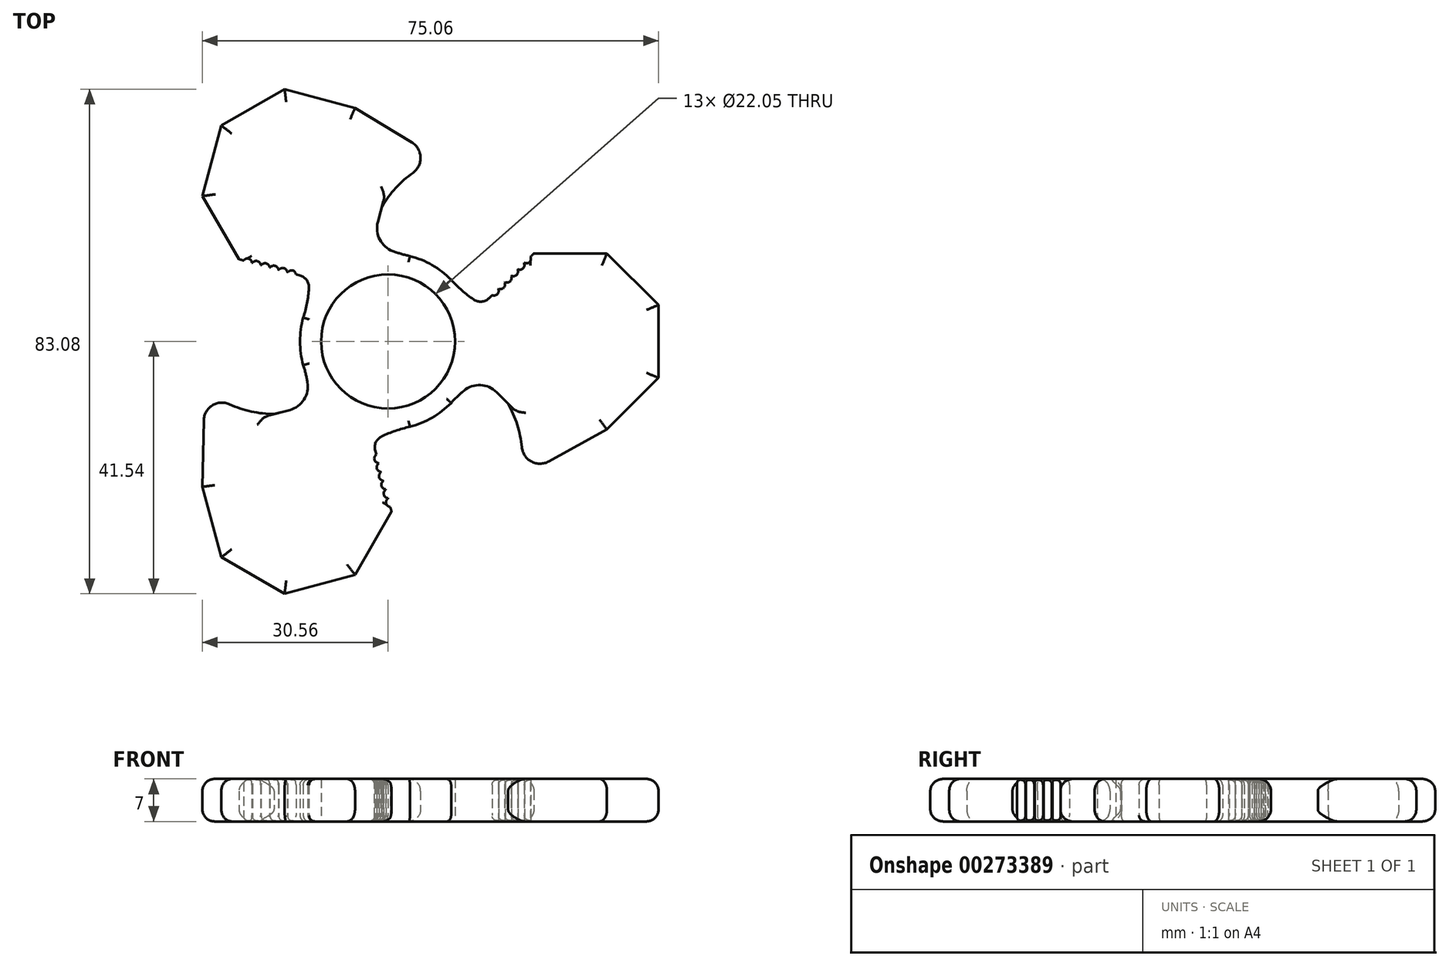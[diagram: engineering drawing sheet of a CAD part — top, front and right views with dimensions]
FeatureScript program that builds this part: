
annotation { "Feature Type Name" : "Feature", "Feature Type Description" : "" }
export const myFeature = defineFeature(function(context is Context, id is Id, definition is map)
    precondition{}
    {
        {
            var Q0;
            Q0=qCreatedBy(makeId("Top.planeOp"),FACE);
            var sketch = newSketch(context, id + "F0", { "sketchPlane" : qUnion([Q0])});
            skCircle(sketch, "E0", {"center": v(0, 0) * mm, "radius": 11.03 * mm});
            skLineSegment(sketch, "E1", {"start": v(30, 25.22) * mm, "end": v(30, -27.35) * mm, "construction": true});
            skCircle(sketch, "E2.cCircle", {"center": v(30, 0) * mm, "radius": 14.5 * mm, "construction": true});
            skLineSegment(sketch, "E2.2", {"start": v(24, 14.5) * mm, "end": v(36, 14.5) * mm});
            skLineSegment(sketch, "E2.3", {"start": v(36, 14.5) * mm, "end": v(44.5, 6) * mm});
            skLineSegment(sketch, "E2.4", {"start": v(44.5, 6) * mm, "end": v(44.5, -6) * mm});
            skLineSegment(sketch, "E2.5", {"start": v(44.5, -6) * mm, "end": v(36, -14.5) * mm});
            skLineSegment(sketch, "E2.7", {"start": v(19.75, -10.25) * mm, "end": v(17.86, -8.36) * mm});
            skPoint(sketch, "E2.0.midPoint", {"position": v(15.5, 0) * mm});
            skLineSegment(sketch, "E3", {"start": v(15.5, 6.36) * mm, "end": v(23.64, 14.5) * mm, "construction": true});
            skArc(sketch, "E4", {"start": v(17.12, 7.63) * mm, "mid": v(17.97, 7.77) * mm, "end": v(18.12, 8.63) * mm});
            skArc(sketch, "E5", {"start": v(18.18, 8.69) * mm, "mid": v(19.04, 8.83) * mm, "end": v(19.18, 9.69) * mm});
            skArc(sketch, "E6", {"start": v(19.24, 9.75) * mm, "mid": v(20.1, 9.9) * mm, "end": v(20.24, 10.75) * mm});
            skArc(sketch, "E7", {"start": v(20.3, 10.8) * mm, "mid": v(21.16, 10.96) * mm, "end": v(21.3, 11.8) * mm});
            skArc(sketch, "E8", {"start": v(21.36, 11.87) * mm, "mid": v(22.22, 12.02) * mm, "end": v(22.36, 12.87) * mm});
            skArc(sketch, "E9", {"start": v(22.42, 12.93) * mm, "mid": v(23.28, 13.08) * mm, "end": v(23.42, 13.93) * mm});
            skLineSegment(sketch, "E10.trimOffspring", {"start": v(18.12, 8.63) * mm, "end": v(18.18, 8.69) * mm});
            skLineSegment(sketch, "E11.trimOffspring", {"start": v(21.3, 11.8) * mm, "end": v(21.36, 11.87) * mm});
            skLineSegment(sketch, "E12.trimOffspring", {"start": v(22.36, 12.87) * mm, "end": v(22.42, 12.93) * mm});
            skLineSegment(sketch, "E13.trimOffspring", {"start": v(20.24, 10.75) * mm, "end": v(20.3, 10.8) * mm});
            skLineSegment(sketch, "E14.trimOffspring", {"start": v(19.18, 9.69) * mm, "end": v(19.24, 9.75) * mm});
            skLineSegment(sketch, "E15.trimOffspring", {"start": v(23.42, 13.93) * mm, "end": v(24, 14.5) * mm});
            skLineSegment(sketch, "E16", {"start": v(36, -14.5) * mm, "end": v(26.43, -19.76) * mm});
            skArc(sketch, "E17", {"start": v(22, -17.43) * mm, "mid": v(21.24, -13.73) * mm, "end": v(19.75, -10.25) * mm});
            skPoint(sketch, "E18.visualSharp", {"position": v(21.86, -22.27) * mm});
            skArc(sketch, "E18.filletArc", {"start": v(22, -17.43) * mm, "mid": v(23.6, -19.78) * mm, "end": v(26.43, -19.76) * mm});
            skPoint(sketch, "E19.orphan", {"position": v(24, -14.5) * mm});
            skArc(sketch, "E20", {"start": v(10.37, 10.14) * mm, "mid": v(6.97, 12.71) * mm, "end": v(2.98, 14.2) * mm});
            skArc(sketch, "E21", {"start": v(10.37, 10.14) * mm, "mid": v(12.13, 8.4) * mm, "end": v(14.08, 6.9) * mm});
            skArc(sketch, "E22.MirrorCS", {"start": v(10.37, -10.14) * mm, "mid": v(11.38, -9.1) * mm, "end": v(12.46, -8.12) * mm});
            skPoint(sketch, "E23.1.0", {"position": v(0.56, 28.03) * mm});
            skArc(sketch, "E23.1.1", {"start": v(4.1, 27.77) * mm, "mid": v(1.27, 25.26) * mm, "end": v(-1, 22.23) * mm});
            skLineSegment(sketch, "E23.1.2", {"start": v(-5.45, 38.43) * mm, "end": v(3.9, 32.77) * mm});
            skCircle(sketch, "E23.1.3", {"center": v(-15, 25.98) * mm, "radius": 14.5 * mm, "construction": true});
            skArc(sketch, "E23.1.4", {"start": v(3.6, 14.05) * mm, "mid": v(2.18, 14.4) * mm, "end": v(0.8, 14.86) * mm});
            skArc(sketch, "E23.1.5", {"start": v(4.1, 27.77) * mm, "mid": v(5.34, 30.33) * mm, "end": v(3.9, 32.77) * mm});
            skPoint(sketch, "E23.1.6", {"position": v(-7.75, 13.42) * mm});
            skPoint(sketch, "E23.1.7", {"position": v(8.36, 30.07) * mm});
            skLineSegment(sketch, "E23.1.8", {"start": v(-36.84, 13.37) * mm, "end": v(8.69, 39.66) * mm, "construction": true});
            skLineSegment(sketch, "E23.1.10", {"start": v(-24.55, 13.53) * mm, "end": v(-30.56, 23.93) * mm});
            skLineSegment(sketch, "E23.1.11", {"start": v(-1, 22.23) * mm, "end": v(-1.69, 19.65) * mm});
            skArc(sketch, "E23.1.12", {"start": v(-13.96, 3.91) * mm, "mid": v(-13.35, 6.3) * mm, "end": v(-13.01, 8.75) * mm});
            skLineSegment(sketch, "E23.1.13", {"start": v(-30.56, 23.93) * mm, "end": v(-27.45, 35.54) * mm});
            skLineSegment(sketch, "E23.1.14", {"start": v(-27.45, 35.54) * mm, "end": v(-17.05, 41.54) * mm});
            skLineSegment(sketch, "E23.1.15", {"start": v(-17.05, 41.54) * mm, "end": v(-5.45, 38.43) * mm});
            skArc(sketch, "E23.1.16", {"start": v(-18.06, 11.8) * mm, "mid": v(-18.62, 12.46) * mm, "end": v(-19.43, 12.16) * mm});
            skLineSegment(sketch, "E23.1.17", {"start": v(-19.43, 12.16) * mm, "end": v(-19.51, 12.18) * mm});
            skLineSegment(sketch, "E23.1.18", {"start": v(-13.26, 10.24) * mm, "end": v(-24.38, 13.22) * mm, "construction": true});
            skArc(sketch, "E23.1.20", {"start": v(-22.41, 12.95) * mm, "mid": v(-22.96, 13.62) * mm, "end": v(-23.78, 13.32) * mm});
            skArc(sketch, "E23.1.22", {"start": v(-15.17, 11.01) * mm, "mid": v(-15.72, 11.68) * mm, "end": v(-16.53, 11.38) * mm});
            skArc(sketch, "E23.1.23", {"start": v(-19.51, 12.18) * mm, "mid": v(-20.07, 12.84) * mm, "end": v(-20.88, 12.54) * mm});
            skLineSegment(sketch, "E23.1.24", {"start": v(-23.78, 13.32) * mm, "end": v(-24.55, 13.53) * mm});
            skArc(sketch, "E23.1.26", {"start": v(-16.62, 11.4) * mm, "mid": v(-17.17, 12.07) * mm, "end": v(-17.98, 11.77) * mm});
            skLineSegment(sketch, "E23.1.27", {"start": v(-17.98, 11.77) * mm, "end": v(-18.06, 11.8) * mm});
            skArc(sketch, "E23.1.28", {"start": v(-20.96, 12.57) * mm, "mid": v(-21.52, 13.23) * mm, "end": v(-22.33, 12.93) * mm});
            skLineSegment(sketch, "E23.1.29", {"start": v(-16.53, 11.38) * mm, "end": v(-16.62, 11.4) * mm});
            skLineSegment(sketch, "E23.1.30", {"start": v(-20.88, 12.54) * mm, "end": v(-20.96, 12.57) * mm});
            skLineSegment(sketch, "E23.1.31", {"start": v(-22.33, 12.93) * mm, "end": v(-22.41, 12.95) * mm});
            skPoint(sketch, "E23.2.0", {"position": v(-24.55, -13.53) * mm});
            skArc(sketch, "E23.2.1", {"start": v(-26.1, -10.34) * mm, "mid": v(-22.5, -11.53) * mm, "end": v(-18.75, -11.97) * mm});
            skLineSegment(sketch, "E23.2.2", {"start": v(-30.56, -23.93) * mm, "end": v(-30.33, -13.01) * mm});
            skCircle(sketch, "E23.2.3", {"center": v(-15, -25.98) * mm, "radius": 14.5 * mm, "construction": true});
            skArc(sketch, "E23.2.4", {"start": v(-13.96, -3.91) * mm, "mid": v(-13.57, -5.3) * mm, "end": v(-13.27, -6.73) * mm});
            skArc(sketch, "E23.2.5", {"start": v(-26.1, -10.34) * mm, "mid": v(-28.93, -10.54) * mm, "end": v(-30.33, -13.01) * mm});
            skPoint(sketch, "E23.2.6", {"position": v(-7.75, -13.42) * mm});
            skPoint(sketch, "E23.2.7", {"position": v(-30.22, -7.8) * mm});
            skLineSegment(sketch, "E23.2.8", {"start": v(6.84, -38.6) * mm, "end": v(-38.69, -12.3) * mm, "construction": true});
            skLineSegment(sketch, "E23.2.10", {"start": v(0.56, -28.03) * mm, "end": v(-5.45, -38.43) * mm});
            skLineSegment(sketch, "E23.2.11", {"start": v(-18.75, -11.97) * mm, "end": v(-16.17, -11.28) * mm});
            skArc(sketch, "E23.2.12", {"start": v(3.6, -14.05) * mm, "mid": v(1.22, -14.71) * mm, "end": v(-1.07, -15.64) * mm});
            skLineSegment(sketch, "E23.2.13", {"start": v(-5.45, -38.43) * mm, "end": v(-17.05, -41.54) * mm});
            skLineSegment(sketch, "E23.2.14", {"start": v(-17.05, -41.54) * mm, "end": v(-27.45, -35.54) * mm});
            skLineSegment(sketch, "E23.2.15", {"start": v(-27.45, -35.54) * mm, "end": v(-30.56, -23.93) * mm});
            skArc(sketch, "E23.2.16", {"start": v(-1.18, -21.54) * mm, "mid": v(-1.48, -22.35) * mm, "end": v(-0.81, -22.9) * mm});
            skLineSegment(sketch, "E23.2.17", {"start": v(-0.81, -22.9) * mm, "end": v(-0.8, -22.99) * mm});
            skLineSegment(sketch, "E23.2.18", {"start": v(-2.24, -16.6) * mm, "end": v(0.74, -27.72) * mm, "construction": true});
            skArc(sketch, "E23.2.20", {"start": v(-0.01, -25.89) * mm, "mid": v(-0.31, -26.7) * mm, "end": v(0.35, -27.25) * mm});
            skArc(sketch, "E23.2.22", {"start": v(-1.96, -18.64) * mm, "mid": v(-2.26, -19.45) * mm, "end": v(-1.59, -20) * mm});
            skArc(sketch, "E23.2.23", {"start": v(-0.8, -22.99) * mm, "mid": v(-1.1, -23.8) * mm, "end": v(-0.42, -24.35) * mm});
            skLineSegment(sketch, "E23.2.24", {"start": v(0.35, -27.25) * mm, "end": v(0.56, -28.03) * mm});
            skArc(sketch, "E23.2.26", {"start": v(-1.57, -20.1) * mm, "mid": v(-1.87, -20.9) * mm, "end": v(-1.2, -21.46) * mm});
            skLineSegment(sketch, "E23.2.27", {"start": v(-1.2, -21.46) * mm, "end": v(-1.18, -21.54) * mm});
            skArc(sketch, "E23.2.28", {"start": v(-0.4, -24.44) * mm, "mid": v(-0.7, -25.25) * mm, "end": v(-0.04, -25.8) * mm});
            skLineSegment(sketch, "E23.2.29", {"start": v(-1.59, -20) * mm, "end": v(-1.57, -20.1) * mm});
            skLineSegment(sketch, "E23.2.30", {"start": v(-0.42, -24.35) * mm, "end": v(-0.4, -24.44) * mm});
            skLineSegment(sketch, "E23.2.31", {"start": v(-0.04, -25.8) * mm, "end": v(-0.01, -25.89) * mm});
            skPoint(sketch, "E24.visualSharp", {"position": v(-2.55, 16.43) * mm});
            skArc(sketch, "E24.filletArc", {"start": v(-1.69, 19.65) * mm, "mid": v(-1.37, 16.77) * mm, "end": v(0.8, 14.86) * mm});
            skPoint(sketch, "E25.visualSharp", {"position": v(-12.95, -10.42) * mm});
            skArc(sketch, "E25.filletArc", {"start": v(-16.17, -11.28) * mm, "mid": v(-13.84, -9.57) * mm, "end": v(-13.27, -6.73) * mm});
            skPoint(sketch, "E26.visualSharp", {"position": v(15.5, -6) * mm});
            skArc(sketch, "E26.filletArc", {"start": v(17.86, -8.36) * mm, "mid": v(15.2, -7.2) * mm, "end": v(12.46, -8.12) * mm});
            skArc(sketch, "E27.trimOffspring", {"start": v(-13.78, 4.52) * mm, "mid": v(-14.5, 0) * mm, "end": v(-13.78, -4.52) * mm});
            skArc(sketch, "E28.trimOffspring", {"start": v(2.98, -14.2) * mm, "mid": v(6.97, -12.71) * mm, "end": v(10.37, -10.14) * mm});
            skPoint(sketch, "E29.visualSharp", {"position": v(15.5, 6) * mm});
            skArc(sketch, "E29.filletArc", {"start": v(14.08, 6.9) * mm, "mid": v(15.4, 6.56) * mm, "end": v(16.63, 7.13) * mm});
            skPoint(sketch, "E30.center.orphan", {"position": v(16.38, 7.24) * mm});
            skPoint(sketch, "E31.visualSharp", {"position": v(-2.55, -16.43) * mm});
            skArc(sketch, "E31.filletArc", {"start": v(-1.07, -15.64) * mm, "mid": v(-2.02, -16.61) * mm, "end": v(-2.14, -17.97) * mm});
            skLineSegment(sketch, "E32", {"start": v(-2.14, -17.97) * mm, "end": v(-1.96, -18.64) * mm});
            skLineSegment(sketch, "E33", {"start": v(16.63, 7.13) * mm, "end": v(17.12, 7.63) * mm});
            skPoint(sketch, "E34.visualSharp", {"position": v(-12.95, 10.42) * mm});
            skArc(sketch, "E34.filletArc", {"start": v(-13.01, 8.75) * mm, "mid": v(-13.38, 10.06) * mm, "end": v(-14.5, 10.83) * mm});
            skLineSegment(sketch, "E35", {"start": v(-14.5, 10.83) * mm, "end": v(-15.17, 11.01) * mm});
            skSolve(sketch);
        }
        {
            var Q0;
            Q0=makeQuery(id+"F0.imprint","IMPRINT",FACE,{"disambiguationData":[TD([[makeQuery(id+"F0.imprint","IMPRINT",EDGE,{"derivedFrom":sQuery(id+"F0.wireOp",EDGE,"E0")}),-1.0]])]});
            extrude(context, id + "F1", {"entities" : qUnion([Q0]), "depth" : 7 * mm});
        }
        {
            var Q0;
            Q0=makeQuery(id+"F1.opExtrude","CAP_EDGE",EDGE,{"disambiguationData":[OSD([sQuery(id+"F0.wireOp",EDGE,"E23.1.13")])],"isStart":false});
            var Q1;
            Q1=makeQuery(id+"F1.opExtrude","CAP_EDGE",EDGE,{"disambiguationData":[OSD([sQuery(id+"F0.wireOp",EDGE,"E23.1.14")])],"isStart":false});
            var Q2;
            Q2=makeQuery(id+"F1.opExtrude","CAP_EDGE",EDGE,{"disambiguationData":[OSD([sQuery(id+"F0.wireOp",EDGE,"E23.1.15")])],"isStart":false});
            var Q3;
            Q3=makeQuery(id+"F1.opExtrude","CAP_EDGE",EDGE,{"disambiguationData":[OSD([sQuery(id+"F0.wireOp",EDGE,"E23.2.14")])],"isStart":false});
            var Q4;
            Q4=makeQuery(id+"F1.opExtrude","CAP_EDGE",EDGE,{"disambiguationData":[OSD([sQuery(id+"F0.wireOp",EDGE,"E23.2.13")])],"isStart":false});
            var Q5;
            Q5=makeQuery(id+"F1.opExtrude","CAP_EDGE",EDGE,{"disambiguationData":[OSD([sQuery(id+"F0.wireOp",EDGE,"E23.2.15")])],"isStart":false});
            var Q6;
            Q6=makeQuery(id+"F1.opExtrude","CAP_EDGE",EDGE,{"disambiguationData":[OSD([sQuery(id+"F0.wireOp",EDGE,"E23.1.10")])],"isStart":false});
            var Q7;
            Q7=makeQuery(id+"F1.opExtrude","CAP_EDGE",EDGE,{"disambiguationData":[OSD([sQuery(id+"F0.wireOp",EDGE,"E23.2.10")])],"isStart":false});
            var Q8;
            Q8=makeQuery(id+"F1.opExtrude","CAP_EDGE",EDGE,{"disambiguationData":[OSD([sQuery(id+"F0.wireOp",EDGE,"E16")])],"isStart":false});
            var Q9;
            Q9=makeQuery(id+"F1.opExtrude","CAP_EDGE",EDGE,{"disambiguationData":[OSD([sQuery(id+"F0.wireOp",EDGE,"E2.5")])],"isStart":false});
            var Q10;
            Q10=makeQuery(id+"F1.opExtrude","CAP_EDGE",EDGE,{"disambiguationData":[OSD([sQuery(id+"F0.wireOp",EDGE,"E23.2.2")])],"isStart":false});
            var Q11;
            Q11=makeQuery(id+"F1.opExtrude","CAP_EDGE",EDGE,{"disambiguationData":[OSD([sQuery(id+"F0.wireOp",EDGE,"E23.1.2")])],"isStart":false});
            var Q12;
            Q12=makeQuery(id+"F1.opExtrude","CAP_EDGE",EDGE,{"disambiguationData":[OSD([sQuery(id+"F0.wireOp",EDGE,"E2.4")])],"isStart":false});
            var Q13;
            Q13=makeQuery(id+"F1.opExtrude","CAP_EDGE",EDGE,{"disambiguationData":[OSD([sQuery(id+"F0.wireOp",EDGE,"E2.3")])],"isStart":false});
            var Q14;
            Q14=makeQuery(id+"F1.opExtrude","CAP_EDGE",EDGE,{"disambiguationData":[OSD([sQuery(id+"F0.wireOp",EDGE,"E2.2")])],"isStart":false});
            var Q15;
            Q15=makeQuery(id+"F1.opExtrude","CAP_EDGE",EDGE,{"disambiguationData":[OSD([sQuery(id+"F0.wireOp",EDGE,"E23.1.2")])],"isStart":true});
            var Q16;
            Q16=makeQuery(id+"F1.opExtrude","CAP_EDGE",EDGE,{"disambiguationData":[OSD([sQuery(id+"F0.wireOp",EDGE,"E23.1.15")])],"isStart":true});
            var Q17;
            Q17=makeQuery(id+"F1.opExtrude","CAP_EDGE",EDGE,{"disambiguationData":[OSD([sQuery(id+"F0.wireOp",EDGE,"E23.1.14")])],"isStart":true});
            var Q18;
            Q18=makeQuery(id+"F1.opExtrude","CAP_EDGE",EDGE,{"disambiguationData":[OSD([sQuery(id+"F0.wireOp",EDGE,"E23.1.13")])],"isStart":true});
            var Q19;
            Q19=makeQuery(id+"F1.opExtrude","CAP_EDGE",EDGE,{"disambiguationData":[OSD([sQuery(id+"F0.wireOp",EDGE,"E23.1.10")])],"isStart":true});
            var Q20;
            Q20=makeQuery(id+"F1.opExtrude","CAP_EDGE",EDGE,{"disambiguationData":[OSD([sQuery(id+"F0.wireOp",EDGE,"E23.2.10")])],"isStart":true});
            var Q21;
            Q21=makeQuery(id+"F1.opExtrude","CAP_EDGE",EDGE,{"disambiguationData":[OSD([sQuery(id+"F0.wireOp",EDGE,"E23.2.13")])],"isStart":true});
            var Q22;
            Q22=makeQuery(id+"F1.opExtrude","CAP_EDGE",EDGE,{"disambiguationData":[OSD([sQuery(id+"F0.wireOp",EDGE,"E23.2.14")])],"isStart":true});
            var Q23;
            Q23=makeQuery(id+"F1.opExtrude","CAP_EDGE",EDGE,{"disambiguationData":[OSD([sQuery(id+"F0.wireOp",EDGE,"E23.2.15")])],"isStart":true});
            var Q24;
            Q24=makeQuery(id+"F1.opExtrude","CAP_EDGE",EDGE,{"disambiguationData":[OSD([sQuery(id+"F0.wireOp",EDGE,"E23.2.2")])],"isStart":true});
            var Q25;
            Q25=makeQuery(id+"F1.opExtrude","CAP_EDGE",EDGE,{"disambiguationData":[OSD([sQuery(id+"F0.wireOp",EDGE,"E16")])],"isStart":true});
            var Q26;
            Q26=makeQuery(id+"F1.opExtrude","CAP_EDGE",EDGE,{"disambiguationData":[OSD([sQuery(id+"F0.wireOp",EDGE,"E2.5")])],"isStart":true});
            var Q27;
            Q27=makeQuery(id+"F1.opExtrude","CAP_EDGE",EDGE,{"disambiguationData":[OSD([sQuery(id+"F0.wireOp",EDGE,"E2.4")])],"isStart":true});
            var Q28;
            Q28=makeQuery(id+"F1.opExtrude","CAP_EDGE",EDGE,{"disambiguationData":[OSD([sQuery(id+"F0.wireOp",EDGE,"E2.3")])],"isStart":true});
            var Q29;
            Q29=makeQuery(id+"F1.opExtrude","CAP_EDGE",EDGE,{"disambiguationData":[OSD([sQuery(id+"F0.wireOp",EDGE,"E2.2")])],"isStart":true});
            fillet(context, id + "F2", {"entities" : qUnion([Q0, Q1, Q2, Q3, Q4, Q5, Q6, Q7, Q8, Q9, Q10, Q11, Q12, Q13, Q14, Q15, Q16, Q17, Q18, Q19, Q20, Q21, Q22, Q23, Q24, Q25, Q26, Q27, Q28, Q29]), "radius" : 2 * mm, "tangentPropagation" : true, "allowEdgeOverflow" : false});
        }
        {
            var Q0;
            Q0=makeQuery(id+"F1.opExtrude","CAP_EDGE",EDGE,{"disambiguationData":[OSD([sQuery(id+"F0.wireOp",EDGE,"E20")])],"isStart":false});
            var Q1;
            Q1=makeQuery(id+"F1.opExtrude","CAP_EDGE",EDGE,{"disambiguationData":[OSD([sQuery(id+"F0.wireOp",EDGE,"E28.trimOffspring")])],"isStart":false});
            var Q2;
            Q2=makeQuery(id+"F1.opExtrude","CAP_EDGE",EDGE,{"disambiguationData":[OSD([sQuery(id+"F0.wireOp",EDGE,"E27.trimOffspring")])],"isStart":false});
            var Q3;
            Q3=makeQuery(id+"F1.opExtrude","CAP_EDGE",EDGE,{"disambiguationData":[OSD([sQuery(id+"F0.wireOp",EDGE,"E23.1.12")])],"isStart":false});
            var Q4;
            Q4=makeQuery(id+"F1.opExtrude","CAP_EDGE",EDGE,{"disambiguationData":[OSD([sQuery(id+"F0.wireOp",EDGE,"E23.2.4")])],"isStart":false});
            var Q5;
            Q5=makeQuery(id+"F1.opExtrude","CAP_EDGE",EDGE,{"disambiguationData":[OSD([sQuery(id+"F0.wireOp",EDGE,"E23.2.12")])],"isStart":false});
            var Q6;
            Q6=makeQuery(id+"F1.opExtrude","CAP_EDGE",EDGE,{"disambiguationData":[OSD([sQuery(id+"F0.wireOp",EDGE,"E22.MirrorCS")])],"isStart":false});
            var Q7;
            Q7=makeQuery(id+"F1.opExtrude","CAP_EDGE",EDGE,{"disambiguationData":[OSD([sQuery(id+"F0.wireOp",EDGE,"E21")])],"isStart":false});
            var Q8;
            Q8=makeQuery(id+"F1.opExtrude","CAP_EDGE",EDGE,{"disambiguationData":[OSD([sQuery(id+"F0.wireOp",EDGE,"E23.1.4")])],"isStart":false});
            var Q9;
            Q9=makeQuery(id+"F1.opExtrude","CAP_EDGE",EDGE,{"disambiguationData":[OSD([sQuery(id+"F0.wireOp",EDGE,"E20")])],"isStart":true});
            var Q10;
            Q10=makeQuery(id+"F1.opExtrude","CAP_EDGE",EDGE,{"disambiguationData":[OSD([sQuery(id+"F0.wireOp",EDGE,"E21")])],"isStart":true});
            var Q11;
            Q11=makeQuery(id+"F1.opExtrude","CAP_EDGE",EDGE,{"disambiguationData":[OSD([sQuery(id+"F0.wireOp",EDGE,"E23.1.4")])],"isStart":true});
            var Q12;
            Q12=makeQuery(id+"F1.opExtrude","CAP_EDGE",EDGE,{"disambiguationData":[OSD([sQuery(id+"F0.wireOp",EDGE,"E23.1.12")])],"isStart":true});
            var Q13;
            Q13=makeQuery(id+"F1.opExtrude","CAP_EDGE",EDGE,{"disambiguationData":[OSD([sQuery(id+"F0.wireOp",EDGE,"E27.trimOffspring")])],"isStart":true});
            var Q14;
            Q14=makeQuery(id+"F1.opExtrude","CAP_EDGE",EDGE,{"disambiguationData":[OSD([sQuery(id+"F0.wireOp",EDGE,"E23.2.4")])],"isStart":true});
            var Q15;
            Q15=makeQuery(id+"F1.opExtrude","CAP_EDGE",EDGE,{"disambiguationData":[OSD([sQuery(id+"F0.wireOp",EDGE,"E23.2.12")])],"isStart":true});
            var Q16;
            Q16=makeQuery(id+"F1.opExtrude","CAP_EDGE",EDGE,{"disambiguationData":[OSD([sQuery(id+"F0.wireOp",EDGE,"E28.trimOffspring")])],"isStart":true});
            var Q17;
            Q17=makeQuery(id+"F1.opExtrude","CAP_EDGE",EDGE,{"disambiguationData":[OSD([sQuery(id+"F0.wireOp",EDGE,"E22.MirrorCS")])],"isStart":true});
            fillet(context, id + "F3", {"entities" : qUnion([Q0, Q1, Q2, Q3, Q4, Q5, Q6, Q7, Q8, Q9, Q10, Q11, Q12, Q13, Q14, Q15, Q16, Q17]), "radius" : 1 * mm, "tangentPropagation" : true, "allowEdgeOverflow" : false});
        }
    });
